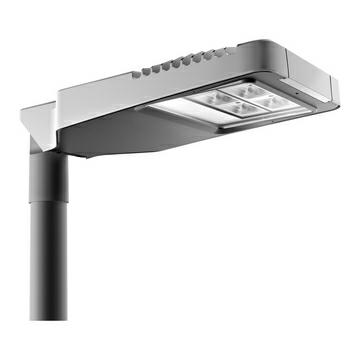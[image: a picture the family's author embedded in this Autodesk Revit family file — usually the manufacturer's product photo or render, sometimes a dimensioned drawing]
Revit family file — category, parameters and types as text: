
# Revit family: Lighting-Stradale-GEWISS-ROAD[5]MEDIUM-LED_OTTICA_WIDE-W_CLII
name_source: partatom
category: Apparecchi per illuminazione
units: mm (PartAtom-declared; Revit-internal decimal feet)

## family parameters
Basato su piano di lavoro = No
Condiviso = No
Punto di calcolo locali = No
Quota connettore circolare = Usa diametro
Sempre verticale = Sì
Sorgente d'illuminazione = No
Taglio con vuoti quando caricato = No
Tipo di parte = Normale

## types (1)
- Lighting-Stradale-GEWISS-ROAD[5]MEDIUM-LED_OTTICA_WIDE-W_CLII
    Alimentatore = Incluso
    Apparecchio a ridotta temperatura superficiale = -
    Applicazione = Esterno
    Cablaggio = Sezionatore
    Caratteristiche elettriche e gestione della luce = -
    Caratteristiche ottiche e illuminotecniche = -
    Catalogo = LIGHTING
    Catalogo Serie = ROAD [5]
    Certificazione DIN 18032-3 = -
    Certificazioni e classificazioni = -
    Classe fotobiologica = RG0
    Classe isolamento = II
    Classificazione: = -
    Codice Electrocod = 244C
    Codice digitale univoco (Datamatrix) = Attualmente non presente
    Colore = Grigio grafite
    Contesto = Illuminazione stradale e parcheggi
    Controllo abbagliamento e luminanza = G*4 - ULOR = 0
    Corpo = Alluminio pressofuso
    Corrente di pilotaggio. = 0,5A
    Descrizione = GWR5254BW - ROAD5 MEDI WIDE 4M 4000K 0,50A CL2 BI.W
    Dispositivo di protezione = DM 10KV / CM 10KV
    Distanza minima dall'oggetto illuminato = 1M
    Durata di vita = L90B10 (Tq+25°C) = 100.000 h
    Efficienza luminosa (lm/W) = 110
    Finitura colore = Verniciato a polveri
    Fissaggio = Testa palo - Sbraccio
    Frequenza nominale (Hz) = 50 / 60
    Gancio di chiusura = Maniglia frontale integrata
    Garanzia = 5 anni
    Grado di protezione = IP66
    Gruppo ottico = Riflettore in PC metallizzato
    Guarnizioni = silicone antinvecchiamento
    IDF = 788eb2dc-9d97-4dd6-bce6-a7bae18c43b7
    IDT = 9b7d0eba829245cc99b21f64ea3ca485
    IPEA = STRADALE = A+ // GRANDI AREE = A4+ // CICLOPEDONALI = A+ // AREE VERDI = A+ // CENTRO STORICO = A5+
    Immagine tipo = GWR5276M.jpg
    Inclinazione = -20° ÷ +10° sbraccio - -10° ÷ +20° testa palo
    Indice di resa cromatica = CRI-70
    Informazioni generali = -
    Installazione e manutenzione = -
    LED Life time (L80B10) = 100000H
    Lampada = LED
    Lampada: = LED
    Lumen output (lm) = 16100
    Materiali = -
    Modello = GWR5254BW
    Norma di riferimento = EN 60598-2-3, EN 60598-1 IEC/TR 62778
    Numero moduli = 4 (4x3 LED)
    Ottica = WIDE
    Peso (kg): = 8,4
    Potenza assorbita : = 146 W @ 0.5A
    Potenza di sistema = 146W
    Produttore = GEWISS S.p.A.
    Regolazione inclinazione = -20° ÷ +10° sbraccio - -10° ÷ +20° testa palo
    Resistenza agli urti = IK08
    Resistenza al filo incandescente = -
    Resistenza alle sovratensioni = 10 KV in modalità comune
    SEO = Stradale
    Scheda Tecnica = https://www.gewiss.com
    Schermo = Vetro piano temperato spessore 4mm
    Sistema di controllo = Biregime con autoapprendimento
    Sostituibilità gruppo ottico = Non disponibile
    Sostituibilità piastra di cablaggio = Non disponibile
    Superficie massima esposta al vento = 0,19M2
    Superficie massima esposta al vento : = 0.19 m2
    Temperatura di colore = 4000K
    Temperatura di colore: = 4000 K (CRI>70)
    Temperatura di esercizio = -25 +30 °C
    Temperatura di stoccaggio = -
    Temperatura di utilizzo = -25 +30 °C
    Tensione = 220 / 240 V - 50 / 60 Hz
    Tensione di alimentazione = 220 - 240 V
    Tipo alimentatore = Driver Led in corrente continua
    Tipo di apparecchio = Apparecchiatura stradale a LED
    Tipo di installazione e montaggio = Testa palo - Sbraccio
    Tipologia = Biregime
    Tipologia sorgente luminosa = LED - Non sostituibile
    Tolleranza cromatica = SDCM = 5
    URL = https://www.gewiss.com
    Vano di alimentazione = Integrato
    Versione file RFA = 20.11
    Viti esterne = Acciaio inox

## geometry (parser evidence)
native form markers: Blend x2
no freeform markers — native parametric forms only
